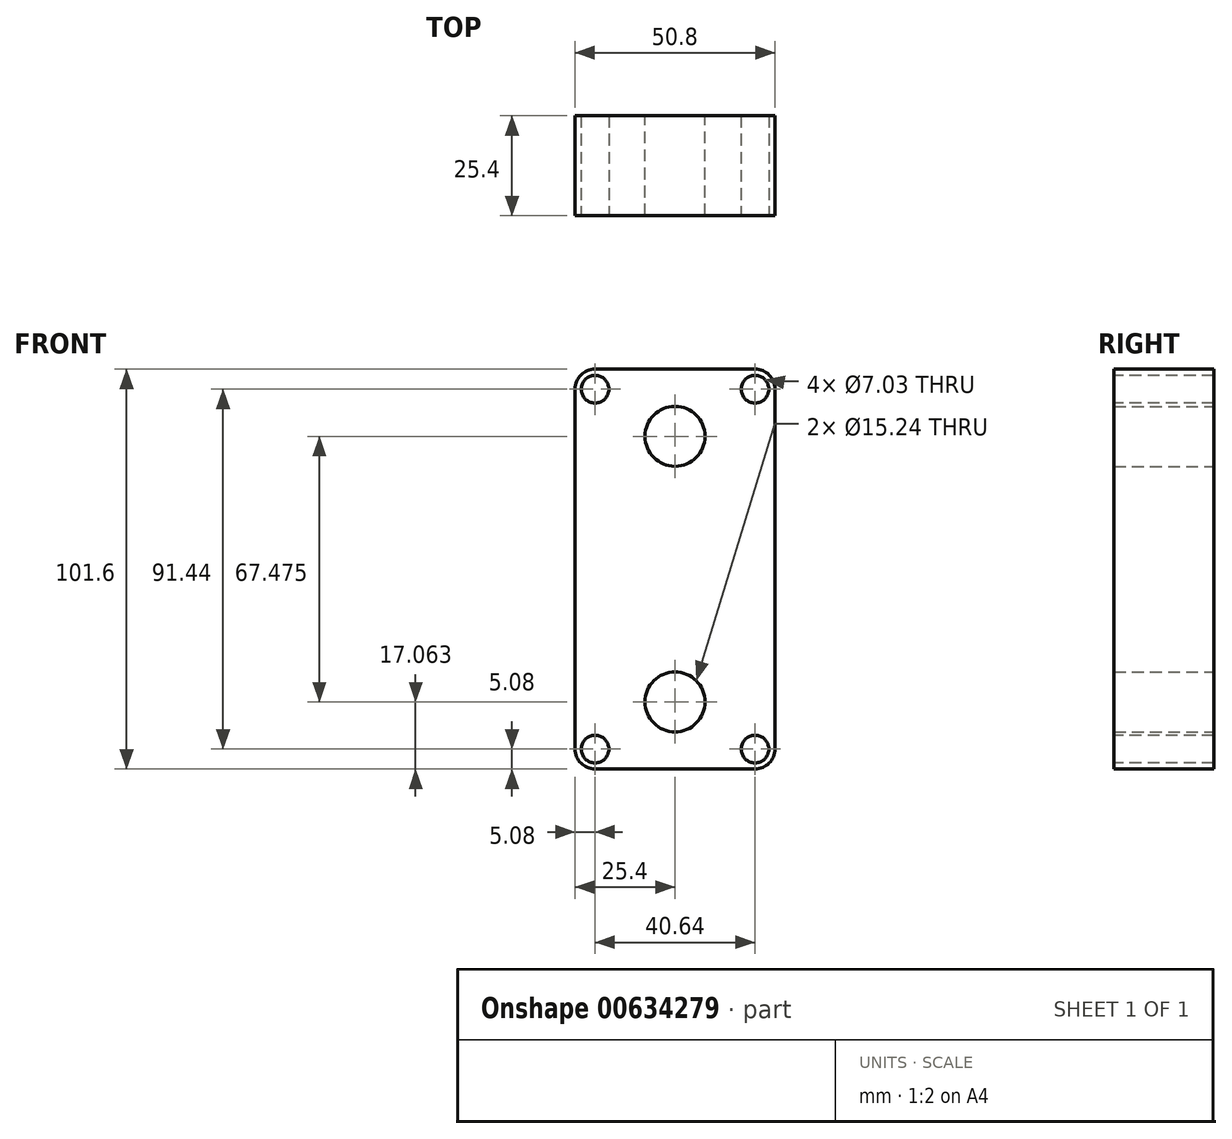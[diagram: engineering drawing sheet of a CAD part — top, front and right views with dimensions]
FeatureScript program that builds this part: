
annotation { "Feature Type Name" : "Feature", "Feature Type Description" : "" }
export const myFeature = defineFeature(function(context is Context, id is Id, definition is map)
    precondition{}
    {
        {
            var Q0;
            Q0=qCreatedBy(makeId("Front.planeOp"),FACE);
            var sketch = newSketch(context, id + "F0", { "sketchPlane" : qUnion([Q0])});
            skLineSegment(sketch, "E0.bottom", {"start": v(25.4, 50.8) * mm, "end": v(-25.4, 50.8) * mm});
            skLineSegment(sketch, "E0.top", {"start": v(25.4, -50.8) * mm, "end": v(-25.4, -50.8) * mm});
            skLineSegment(sketch, "E0.left", {"start": v(25.4, 50.8) * mm, "end": v(25.4, -50.8) * mm});
            skLineSegment(sketch, "E0.right", {"start": v(-25.4, 50.8) * mm, "end": v(-25.4, -50.8) * mm});
            skPoint(sketch, "E0.middle", {"position": v(0, 0) * mm});
            skCircle(sketch, "E1", {"center": v(0, -33.74) * mm, "radius": 7.62 * mm});
            skCircle(sketch, "E2.MirrorC", {"center": v(0, 33.74) * mm, "radius": 7.62 * mm});
            skSolve(sketch);
        }
        {
            var Q0;
            Q0=makeQuery(id+"F0.imprint","IMPRINT",FACE,{"disambiguationData":[TD([[makeQuery(id+"F0.imprint","IMPRINT",EDGE,{"derivedFrom":sQuery(id+"F0.wireOp",EDGE,"E0.bottom")}),1.0]])]});
            extrude(context, id + "F1", {"entities" : qUnion([Q0]), "endBound" : BoundingType.SYMMETRIC, "depth" : 25.4 * mm, "offsetDistance" : 25.4 * mm});
        }
        {
            var Q0;
            Q0=makeQuery(id+"F1.opExtrude","SWEPT_EDGE",EDGE,{"disambiguationData":[OSD([sQuery(id+"F0.wireOp",EDGE,"E0.top"),sQuery(id+"F0.wireOp",EDGE,"E0.left")])]});
            var Q1;
            Q1=makeQuery(id+"F1.opExtrude","SWEPT_EDGE",EDGE,{"disambiguationData":[OSD([sQuery(id+"F0.wireOp",EDGE,"E0.top"),sQuery(id+"F0.wireOp",EDGE,"E0.right")])]});
            var Q2;
            Q2=makeQuery(id+"F1.opExtrude","SWEPT_EDGE",EDGE,{"disambiguationData":[OSD([sQuery(id+"F0.wireOp",EDGE,"E0.bottom"),sQuery(id+"F0.wireOp",EDGE,"E0.left")])]});
            var Q3;
            Q3=makeQuery(id+"F1.opExtrude","SWEPT_EDGE",EDGE,{"disambiguationData":[OSD([sQuery(id+"F0.wireOp",EDGE,"E0.bottom"),sQuery(id+"F0.wireOp",EDGE,"E0.right")])]});
            fillet(context, id + "F2", {"entities" : qUnion([Q0, Q1, Q2, Q3]), "radius" : 5.08 * mm, "tangentPropagation" : true, "allowEdgeOverflow" : false});
        }
        {
            var Q0;
            Q0=makeQuery(id+"F1.opExtrude","CAP_FACE",FACE,{"disambiguationData":[OSD([sQuery(id+"F0.wireOp",EDGE,"E0.bottom"),sQuery(id+"F0.wireOp",EDGE,"E0.top"),sQuery(id+"F0.wireOp",EDGE,"E0.left"),sQuery(id+"F0.wireOp",EDGE,"E0.right"),sQuery(id+"F0.wireOp",EDGE,"E1"),sQuery(id+"F0.wireOp",EDGE,"E2.MirrorC")])],"isStart":false});
            var sketch = newSketch(context, id + "F3", { "sketchPlane" : qUnion([Q0])});
            skCircle(sketch, "E3", {"center": v(-20.32, 45.72) * mm, "radius": 3.52 * mm});
            skCircle(sketch, "E4.MirrorC", {"center": v(-20.32, -45.72) * mm, "radius": 3.52 * mm});
            skCircle(sketch, "E5.MirrorC", {"center": v(20.32, 45.72) * mm, "radius": 3.52 * mm});
            skCircle(sketch, "E6.MirrorC", {"center": v(20.32, -45.72) * mm, "radius": 3.52 * mm});
            skSolve(sketch);
        }
        {
            var Q0;
            Q0 = qSketchRegion(id + "F3", true);
            extrude(context, id + "F4", {"entities" : qUnion([Q0]), "operationType" : NewBodyOperationType.REMOVE, "endBound" : BoundingType.SYMMETRIC, "oppositeDirection" : true, "depth" : 50.8 * mm, "offsetDistance" : 25.4 * mm});
        }
    });
